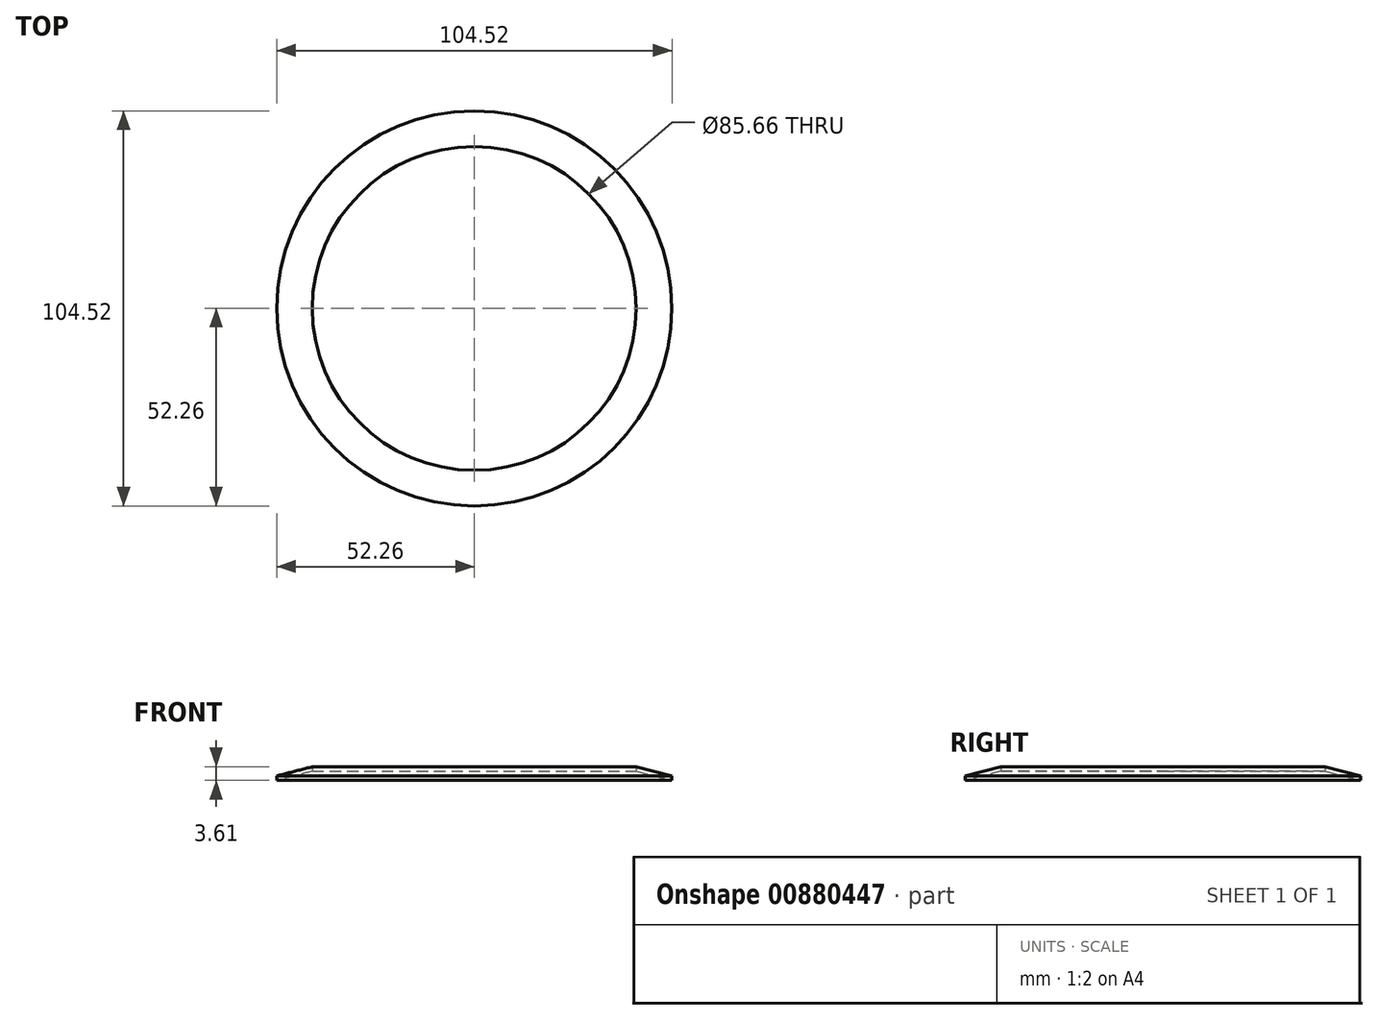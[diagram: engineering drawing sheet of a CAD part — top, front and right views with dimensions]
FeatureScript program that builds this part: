
annotation { "Feature Type Name" : "Feature", "Feature Type Description" : "" }
export const myFeature = defineFeature(function(context is Context, id is Id, definition is map)
    precondition{}
    {
        {
            var Q0;
            Q0=qCreatedBy(makeId("Front.planeOp"),FACE);
            var sketch = newSketch(context, id + "F0", { "sketchPlane" : qUnion([Q0])});
            skLineSegment(sketch, "E0", {"start": v(-52.26, 0) * mm, "end": v(-42.83, 2.45) * mm});
            skLineSegment(sketch, "E1", {"start": v(-42.83, 2.45) * mm, "end": v(-42.83, 3.6) * mm});
            skLineSegment(sketch, "E2", {"start": v(-42.83, 3.6) * mm, "end": v(-52.26, 1.16) * mm});
            skLineSegment(sketch, "E3", {"start": v(-52.26, 1.16) * mm, "end": v(-52.26, 0) * mm});
            skPoint(sketch, "E4", {"position": v(0, 0) * mm});
            skLineSegment(sketch, "E5", {"start": v(0, 0) * mm, "end": v(0, 6.76) * mm});
            skSolve(sketch);
        }
        {
            var Q0;
            Q0 = qSketchRegion(id + "F0", true);
            var Q1;
            Q1=sQuery(id+"F0.wireOp",EDGE,"E5");
            revolve(context, id + "F1", {"surfaceOperationType" : NewSurfaceOperationType.NEW, "entities" : qUnion([Q0]), "axis" : qUnion([Q1]), "revolveType" : RevolveType.FULL});
        }
    });
